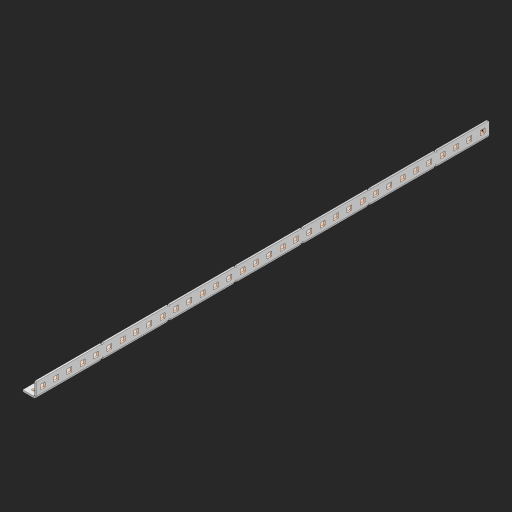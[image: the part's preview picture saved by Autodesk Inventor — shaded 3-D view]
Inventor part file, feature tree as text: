
AUTODESK INVENTOR PART (.ipt)
format: ipt  version: 2023 (Build 270158000, 158)  size: 1,041,408 bytes
history: native  units: in
note: dims shown in document units (in); Inventor stores cm internally (conversion verified against a paired STEP export)
features: other x73, extrude x67, sheet_metal_op x10, sketch x8, mirror x1, pattern_linear x1, chamfer x1
ambient origin geometry x8: Origin, YZ Plane, XZ Plane, XY Plane, X Axis, Y Axis, Z Axis, Center Point
bodies: Solid1 (feature_tree), Body (feature_tree)
feature tree (161):
  other  "Flange Pattern Plane"
  sheet_metal_op  "Flange Pattern"
  sheet_metal_op  "Body Pattern"
  other  "Arc Length"
  mirror  "Notch Mirror"
  pattern_linear  "Notch Pattern"  Spacing1=0.25in  [1 undecoded]
  chamfer  "End Chamfer"
  extrude  "Half Cut"  Depth=0.0625in
  sketch  "Sketch1"  dims[d0=1.5in]
  other  "Plate1"
  sketch  "Sketch2"  dims[d1=17.0in]
  other  "Plate2"
  sheet_metal_op  "Bend1"
  sheet_metal_op  "Corner1"
  sketch  "Sketch3"  dims[d2=0.0625in]
  other  "Flange Pattern Sketch"
  sketch  "Sketch7"  dims[d3=0.0625in]
  other  "Srf1"
  other  "Srf2"
  sketch  "Sketch8"  dims[d4=0.0312in]
  sketch  "Sketch9"  dims[d5=0.125in]
  other  "Srf91"
  sheet_metal_op  "Body Pattern Sketch"
  other  "Srf92"
  sketch  "Sketch13"  dims[d6=0.0625in]
  sketch  "Sketch14"  dims[d7=0.5in d8=90.0deg d9=0.0312in d10=0.25in d11=0.0625in d12=0.0625in d16=0.182in d17=0.02in d18=0.0625in d19=0.0in d20=0.25in d21=0.25in d46=0.172in d47=1.0in d48=0.0in d49=0.182in d50=0.02in d51=0.25in d52=0.25in d53=0.0625in d54=0.0in d55=0.172in d56=1.0in d57=0.0in d60=13.3858in d62=0.5in d63=0.3937in d65=0.5in d85=0.1473in d86=0.1782in d88=0.04in d89=0.0625in d90=0.0in d91=0.04in d92=0.0491in d95=2.5in d96=0.04in d97=0.25in d98=45.0deg d101=0.0in d102=2.497in d131=0.5in d132=13.3858in d134=0.5in d139=0.5in]
  other  "Srf856"
  other  "Srf1310"
  other  "Srf1311"
  other  "Srf1312"
  other  "Srf1376"
  other  "Srf1377"
  other  "Srf1728"
  other  "Srf1755"
  other  "Srf1878"
  other  "Srf1879"
  other  "Srf1880"
  other  "Srf1881"
  other  "Srf1882"
  other  "Srf1883"
  other  "Srf1884"
  other  "Srf1885"
  other  "Srf1886"
  other  "Srf1887"
  other  "Srf1888"
  other  "Srf1889"
  other  "Srf1890"
  other  "Srf1891"
  other  "Srf1892"
  other  "Srf1893"
  other  "Srf1894"
  other  "Srf1895"
  other  "Srf1896"
  other  "Srf1897"
  other  "Srf1898"
  other  "Srf1899"
  other  "Srf1900"
  other  "Srf1901"
  other  "Srf1902"
  other  "Srf1903"
  other  "Srf1904"
  other  "Srf1905"
  other  "Srf1942"
  other  "Srf1943"
  other  "Srf1944"
  other  "Srf1945"
  other  "Srf1946"
  other  "Srf1947"
  other  "Srf1948"
  other  "Srf1949"
  other  "Srf1950"
  other  "Srf1951"
  other  "Srf1952"
  other  "Srf1953"
  other  "Srf1954"
  other  "Srf1955"
  other  "Srf1956"
  other  "Srf1957"
  other  "Srf1958"
  other  "Srf1959"
  other  "Srf1960"
  other  "Srf1961"
  other  "Srf1962"
  other  "Srf1963"
  other  "Srf1964"
  other  "Srf1965"
  other  "Srf1966"
  other  "Srf1967"
  other  "Srf1968"
  other  "Srf1969"
  sheet_metal_op  "Flange Stamp"
  sheet_metal_op  "Flange Circle"
  sheet_metal_op  "Body Stamp"
  sheet_metal_op  "Body Circle"
  sheet_metal_op  "Notch"
  extrude  "ExtrusionSrf2"  Depth=0.0625in
  extrude  "ExtrusionSrf92"  Depth=0.5in
  extrude  "ExtrusionSrf856"  Depth=0.02in
  extrude  "ExtrusionSrf1310"  Depth=0.0625in
  extrude  "ExtrusionSrf1311"  TaperAngle=0.0deg  [1 undecoded]
  extrude  "ExtrusionSrf1312"  Depth=0.5in
  extrude  "ExtrusionSrf1376"  Depth=0.5in
  extrude  "ExtrusionSrf1377"  Depth=0.5in
  extrude  "ExtrusionSrf1728"  Depth=0.5in TaperAngle=0.0deg
  extrude  "ExtrusionSrf1755"  Depth=0.5in
  extrude  "ExtrusionSrf1878"  Depth=0.02in
  extrude  "ExtrusionSrf1879"  Depth=0.5in
  extrude  "ExtrusionSrf1880"  Depth=0.5in
  extrude  "ExtrusionSrf1881"  Depth=0.0625in
  extrude  "ExtrusionSrf1882"  TaperAngle=0.0deg  [1 undecoded]
  extrude  "ExtrusionSrf1883"  Depth=0.5in
  extrude  "ExtrusionSrf1884"  Depth=0.5in TaperAngle=0.0deg
  extrude  "ExtrusionSrf1885"  Depth=0.5in
  extrude  "ExtrusionSrf1886"  Depth=0.5in
  extrude  "ExtrusionSrf1887"  Depth=0.5in
  extrude  "ExtrusionSrf1888"  Depth=0.5in
  extrude  "ExtrusionSrf1889"  Depth=0.5in
  extrude  "ExtrusionSrf1890"  Depth=0.0625in
  extrude  "ExtrusionSrf1891"  TaperAngle=0.0deg  [1 undecoded]
  extrude  "ExtrusionSrf1892"  Depth=0.5in
  extrude  "ExtrusionSrf1893"  Depth=0.5in
  extrude  "ExtrusionSrf1894"  Depth=0.5in
  extrude  "ExtrusionSrf1895"  Depth=0.5in TaperAngle=45.0deg
  extrude  "ExtrusionSrf1896"  TaperAngle=0.0deg  [1 undecoded]
  extrude  "ExtrusionSrf1897"  Depth=0.5in
  extrude  "ExtrusionSrf1898"  Depth=0.5in
  extrude  "ExtrusionSrf1899"  Depth=0.5in
  extrude  "ExtrusionSrf1900"  Depth=0.5in
  extrude  "ExtrusionSrf1901"  Depth=0.5in
  extrude  "ExtrusionSrf1902"  [1 undecoded]
  extrude  "ExtrusionSrf1903"  [1 undecoded]
  extrude  "ExtrusionSrf1904"  [1 undecoded]
  extrude  "ExtrusionSrf1905"  [1 undecoded]
  extrude  "ExtrusionSrf1942"  [1 undecoded]
  extrude  "ExtrusionSrf1943"  [1 undecoded]
  extrude  "ExtrusionSrf1944"  [1 undecoded]
  extrude  "ExtrusionSrf1945"  [1 undecoded]
  extrude  "ExtrusionSrf1946"  [1 undecoded]
  extrude  "ExtrusionSrf1947"  [1 undecoded]
  extrude  "ExtrusionSrf1948"  [1 undecoded]
  extrude  "ExtrusionSrf1949"  [1 undecoded]
  extrude  "ExtrusionSrf1950"  [1 undecoded]
  extrude  "ExtrusionSrf1951"  [1 undecoded]
  extrude  "ExtrusionSrf1952"  [1 undecoded]
  extrude  "ExtrusionSrf1953"  [1 undecoded]
  extrude  "ExtrusionSrf1954"  [1 undecoded]
  extrude  "ExtrusionSrf1955"  [1 undecoded]
  extrude  "ExtrusionSrf1956"  [1 undecoded]
  extrude  "ExtrusionSrf1957"  [1 undecoded]
  extrude  "ExtrusionSrf1958"  [1 undecoded]
  extrude  "ExtrusionSrf1959"  [1 undecoded]
  extrude  "ExtrusionSrf1960"  [1 undecoded]
  extrude  "ExtrusionSrf1961"  [1 undecoded]
  extrude  "ExtrusionSrf1962"  [1 undecoded]
  extrude  "ExtrusionSrf1963"  [1 undecoded]
  extrude  "ExtrusionSrf1964"  [1 undecoded]
  extrude  "ExtrusionSrf1965"  [1 undecoded]
  extrude  "ExtrusionSrf1966"  [1 undecoded]
  extrude  "ExtrusionSrf1967"  [1 undecoded]
  extrude  "ExtrusionSrf1968"  [1 undecoded]
  extrude  "ExtrusionSrf1969"  [1 undecoded]
note: 37 required parameter values undecoded (feature->parameter linkage not recoverable at this tier; creation-order binding heuristic only, values carry confidence <= 0.55)
